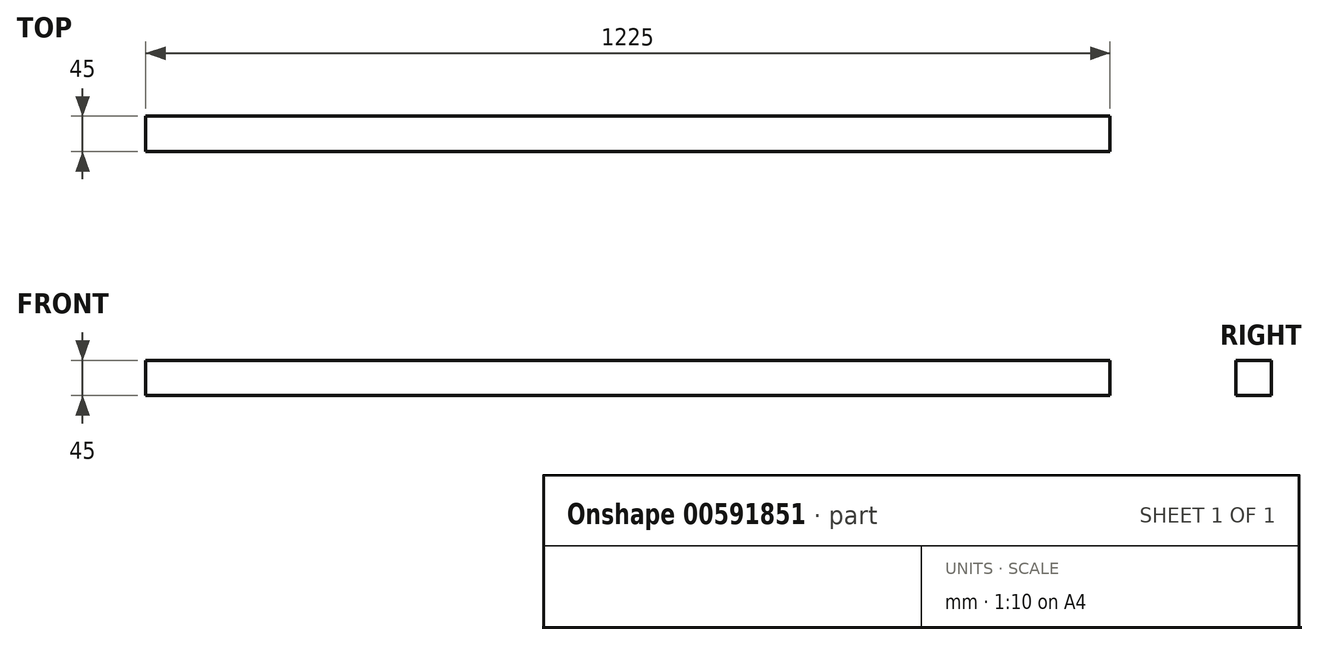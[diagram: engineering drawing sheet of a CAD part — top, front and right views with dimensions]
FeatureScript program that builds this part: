
annotation { "Feature Type Name" : "Feature", "Feature Type Description" : "" }
export const myFeature = defineFeature(function(context is Context, id is Id, definition is map)
    precondition{}
    {
        {
            var Q0;
            Q0=qCreatedBy(makeId("Right.planeOp"),FACE);
            var sketch = newSketch(context, id + "F0", { "sketchPlane" : qUnion([Q0])});
            skLineSegment(sketch, "E0.bottom", {"start": v(0, 0) * mm, "end": v(45, 0) * mm});
            skLineSegment(sketch, "E0.top", {"start": v(0, 45) * mm, "end": v(45, 45) * mm});
            skLineSegment(sketch, "E0.left", {"start": v(0, 0) * mm, "end": v(0, 45) * mm});
            skLineSegment(sketch, "E0.right", {"start": v(45, 0) * mm, "end": v(45, 45) * mm});
            skSolve(sketch);
        }
        {
            var Q0;
            Q0=makeQuery(id+"F0.imprint","IMPRINT",FACE,{"disambiguationData":[TD([[makeQuery(id+"F0.imprint","IMPRINT",EDGE,{"derivedFrom":sQuery(id+"F0.wireOp",EDGE,"E0.bottom")}),1.0]])]});
            extrude(context, id + "F1", {"entities" : qUnion([Q0]), "depth" : 1225 * mm, "offsetDistance" : 25 * mm});
        }
    });
